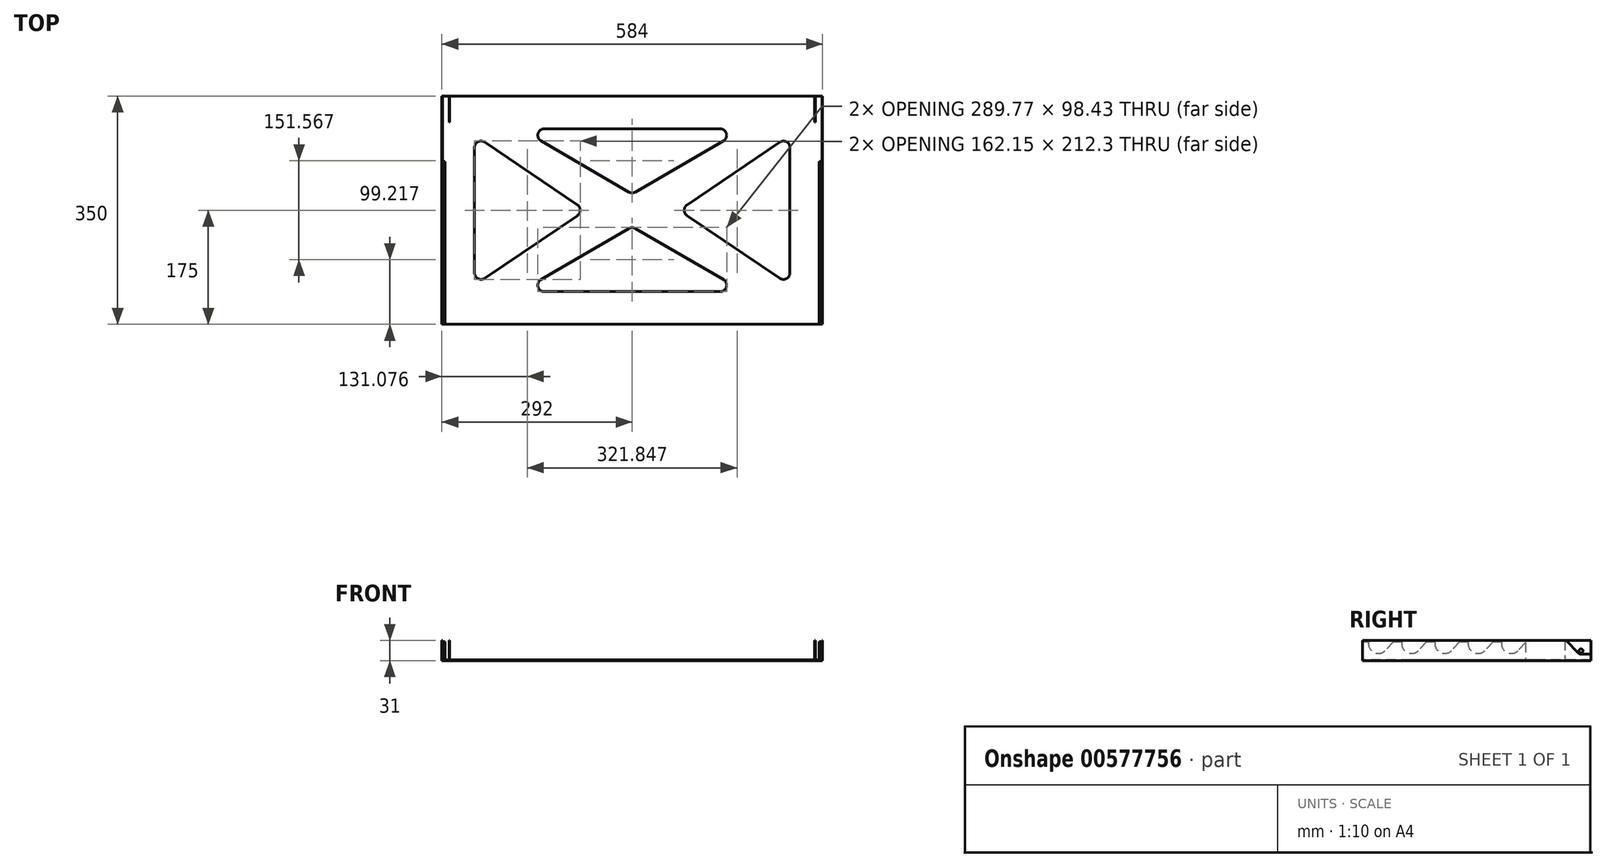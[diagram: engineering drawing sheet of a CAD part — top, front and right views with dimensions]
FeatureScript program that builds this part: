
annotation { "Feature Type Name" : "Feature", "Feature Type Description" : "" }
export const myFeature = defineFeature(function(context is Context, id is Id, definition is map)
    precondition{}
    {
        {
            var Q0;
            Q0=qCreatedBy(makeId("Top.planeOp"),FACE);
            var sketch = newSketch(context, id + "F0", { "sketchPlane" : qUnion([Q0])});
            skLineSegment(sketch, "E0.bottom", {"start": v(-292, 151.73) * mm, "end": v(292, 151.73) * mm});
            skLineSegment(sketch, "E0.top", {"start": v(-292, -198.27) * mm, "end": v(292, -198.27) * mm});
            skLineSegment(sketch, "E0.left", {"start": v(-292, 151.73) * mm, "end": v(-292, -198.27) * mm});
            skLineSegment(sketch, "E0.right", {"start": v(292, 151.73) * mm, "end": v(292, -198.27) * mm});
            skSolve(sketch);
        }
        {
            var Q0;
            Q0 = qSketchRegion(id + "F0", true);
            extrude(context, id + "F1", {"entities" : qUnion([Q0]), "depth" : 1 * mm, "offsetDistance" : 25 * mm});
        }
        {
            var Q0;
            Q0=makeQuery(id+"F1.opExtrude","CAP_FACE",FACE,{"disambiguationData":[OSD([sQuery(id+"F0.wireOp",EDGE,"E0.bottom"),sQuery(id+"F0.wireOp",EDGE,"E0.top"),sQuery(id+"F0.wireOp",EDGE,"E0.left"),sQuery(id+"F0.wireOp",EDGE,"E0.right")])],"isStart":false});
            var sketch = newSketch(context, id + "F2", { "sketchPlane" : qUnion([Q0])});
            skLineSegment(sketch, "E1.bottom", {"start": v(-292, 151.73) * mm, "end": v(-291, 151.73) * mm});
            skLineSegment(sketch, "E1.top", {"start": v(-292, -198.27) * mm, "end": v(-291, -198.27) * mm});
            skLineSegment(sketch, "E1.left", {"start": v(-292, 151.73) * mm, "end": v(-292, -198.27) * mm});
            skLineSegment(sketch, "E1.right", {"start": v(-291, 151.73) * mm, "end": v(-291, -198.27) * mm});
            skLineSegment(sketch, "E2.bottom", {"start": v(292, 151.73) * mm, "end": v(291, 151.73) * mm});
            skLineSegment(sketch, "E2.top", {"start": v(292, -198.27) * mm, "end": v(291, -198.27) * mm});
            skLineSegment(sketch, "E2.left", {"start": v(292, 151.73) * mm, "end": v(292, -198.27) * mm});
            skLineSegment(sketch, "E2.right", {"start": v(291, 151.73) * mm, "end": v(291, -198.27) * mm});
            skSolve(sketch);
        }
        {
            var Q0;
            Q0 = qSketchRegion(id + "F2", true);
            extrude(context, id + "F3", {"entities" : qUnion([Q0]), "operationType" : NewBodyOperationType.ADD, "depth" : 30 * mm, "offsetDistance" : 25 * mm});
        }
        {
            var Q0;
            Q0=makeQuery(id+"F3.boolean.opBoolean","MERGE",FACE,{"derivedFrom":[makeQuery(id+"F1.opExtrude","SWEPT_FACE",FACE,{"disambiguationData":[OSD([sQuery(id+"F0.wireOp",EDGE,"E0.left")])]}),makeQuery(id+"F3.opExtrude","SWEPT_FACE",FACE,{"disambiguationData":[OSD([sQuery(id+"F2.wireOp",EDGE,"E1.left")])]})]});
            var sketch = newSketch(context, id + "F4", { "sketchPlane" : qUnion([Q0])});
            skCircle(sketch, "E3", {"center": v(-136.73, 15) * mm, "radius": 5 * mm});
            skLineSegment(sketch, "E4", {"start": v(-136.73, 15) * mm, "end": v(-136.73, 10) * mm});
            skLineSegment(sketch, "E5", {"start": v(-136.73, 10) * mm, "end": v(-151.73, 10) * mm});
            skLineSegment(sketch, "E6", {"start": v(-151.73, 10) * mm, "end": v(-151.73, 31) * mm});
            skLineSegment(sketch, "E7", {"start": v(-136.73, 15) * mm, "end": v(-120.73, 31) * mm});
            skLineSegment(sketch, "E8", {"start": v(-120.73, 31) * mm, "end": v(-151.73, 31) * mm});
            skLineSegment(sketch, "E9", {"start": v(-133.04, 11.62) * mm, "end": v(-113.67, 31) * mm});
            skSolve(sketch);
        }
        {
            var Q0;
            Q0 = qSketchRegion(id + "F4", true);
            var Q1;
            {var subQ0=sQuery(id+"F4.wireOp",EDGE,"E9");Q1=makeQuery(id+"F4.imprint","IMPRINT",FACE,{"disambiguationData":[TD([[makeQuery(id+"F4.imprint","IMPRINT",EDGE,{"derivedFrom":subQ0}),1.0]])]});}
            extrude(context, id + "F5", {"entities" : qUnion([Q0, Q1]), "operationType" : NewBodyOperationType.REMOVE, "oppositeDirection" : true, "depth" : 645 * mm, "offsetDistance" : 25 * mm});
        }
        {
            var Q0;
            Q0=makeQuery(id+"F1.opExtrude","CAP_FACE",FACE,{"disambiguationData":[OSD([sQuery(id+"F0.wireOp",EDGE,"E0.bottom"),sQuery(id+"F0.wireOp",EDGE,"E0.top"),sQuery(id+"F0.wireOp",EDGE,"E0.left"),sQuery(id+"F0.wireOp",EDGE,"E0.right")])],"isStart":false});
            var sketch = newSketch(context, id + "F6", { "sketchPlane" : qUnion([Q0])});
            skLineSegment(sketch, "E10.bottom", {"start": v(-281, 151.73) * mm, "end": v(-280, 151.73) * mm});
            skLineSegment(sketch, "E10.top", {"start": v(-281, 111.73) * mm, "end": v(-280, 111.73) * mm});
            skLineSegment(sketch, "E10.left", {"start": v(-281, 151.73) * mm, "end": v(-281, 111.73) * mm});
            skLineSegment(sketch, "E10.right", {"start": v(-280, 151.73) * mm, "end": v(-280, 111.73) * mm});
            skLineSegment(sketch, "E11.bottom", {"start": v(281, 151.73) * mm, "end": v(280, 151.73) * mm});
            skLineSegment(sketch, "E11.top", {"start": v(281, 111.73) * mm, "end": v(280, 111.73) * mm});
            skLineSegment(sketch, "E11.left", {"start": v(281, 151.73) * mm, "end": v(281, 111.73) * mm});
            skLineSegment(sketch, "E11.right", {"start": v(280, 151.73) * mm, "end": v(280, 111.73) * mm});
            skSolve(sketch);
        }
        {
            var Q0;
            Q0 = qSketchRegion(id + "F6", true);
            extrude(context, id + "F7", {"entities" : qUnion([Q0]), "operationType" : NewBodyOperationType.ADD, "depth" : 30 * mm, "offsetDistance" : 25 * mm});
        }
        {
            var Q0;
            Q0=makeQuery(id+"F7.opExtrude","SWEPT_FACE",FACE,{"disambiguationData":[OSD([sQuery(id+"F6.wireOp",EDGE,"E10.left")])]});
            var sketch = newSketch(context, id + "F8", { "sketchPlane" : qUnion([Q0])});
            skCircle(sketch, "E12", {"center": v(-136.73, 15) * mm, "radius": 3 * mm});
            skSolve(sketch);
        }
        {
            var Q0;
            Q0 = qSketchRegion(id + "F8", true);
            extrude(context, id + "F9", {"entities" : qUnion([Q0]), "operationType" : NewBodyOperationType.REMOVE, "oppositeDirection" : true, "depth" : 565 * mm, "offsetDistance" : 25 * mm});
        }
        {
            var Q0;
            Q0=makeQuery(id+"F1.opExtrude","CAP_FACE",FACE,{"disambiguationData":[OSD([sQuery(id+"F0.wireOp",EDGE,"E0.bottom"),sQuery(id+"F0.wireOp",EDGE,"E0.top"),sQuery(id+"F0.wireOp",EDGE,"E0.left"),sQuery(id+"F0.wireOp",EDGE,"E0.right")])],"isStart":false});
            var sketch = newSketch(context, id + "F10", { "sketchPlane" : qUnion([Q0])});
            skLineSegment(sketch, "E13.bottom", {"start": v(-290, -198.27) * mm, "end": v(-287, -198.27) * mm});
            skLineSegment(sketch, "E13.top", {"start": v(-290, 51.73) * mm, "end": v(-287, 51.73) * mm});
            skLineSegment(sketch, "E13.left", {"start": v(-290, -198.27) * mm, "end": v(-290, 51.73) * mm});
            skLineSegment(sketch, "E13.right", {"start": v(-287, -198.27) * mm, "end": v(-287, 51.73) * mm});
            skLineSegment(sketch, "E14.bottom", {"start": v(290, -198.27) * mm, "end": v(287, -198.27) * mm});
            skLineSegment(sketch, "E14.top", {"start": v(290, 51.73) * mm, "end": v(287, 51.73) * mm});
            skLineSegment(sketch, "E14.left", {"start": v(290, -198.27) * mm, "end": v(290, 51.73) * mm});
            skLineSegment(sketch, "E14.right", {"start": v(287, -198.27) * mm, "end": v(287, 51.73) * mm});
            skSolve(sketch);
        }
        {
            var Q0;
            Q0 = qSketchRegion(id + "F10", true);
            extrude(context, id + "F11", {"entities" : qUnion([Q0]), "operationType" : NewBodyOperationType.ADD, "depth" : 28 * mm, "offsetDistance" : 25 * mm});
        }
        {
            var Q0;
            Q0=qCreatedBy(makeId("Right.planeOp"),FACE);
            var sketch = newSketch(context, id + "F12", { "sketchPlane" : qUnion([Q0])});
            skCircle(sketch, "E15", {"center": v(-174.38, 26) * mm, "radius": 15 * mm});
            skLineSegment(sketch, "E16", {"start": v(-163.45, 15.73) * mm, "end": v(-125.93, 55.64) * mm});
            skLineSegment(sketch, "E17", {"start": v(-125.93, 55.64) * mm, "end": v(-178.3, 40.48) * mm});
            skCircle(sketch, "E18.1.0.0", {"center": v(-123.38, 26) * mm, "radius": 15 * mm});
            skLineSegment(sketch, "E18.1.0.1", {"start": v(-112.45, 15.73) * mm, "end": v(-74.93, 55.64) * mm});
            skLineSegment(sketch, "E18.1.0.2", {"start": v(-74.93, 55.64) * mm, "end": v(-127.3, 40.48) * mm});
            skCircle(sketch, "E18.2.0.0", {"center": v(-72.38, 26) * mm, "radius": 15 * mm});
            skLineSegment(sketch, "E18.2.0.1", {"start": v(-61.45, 15.73) * mm, "end": v(-23.93, 55.64) * mm});
            skLineSegment(sketch, "E18.2.0.2", {"start": v(-23.93, 55.64) * mm, "end": v(-76.3, 40.48) * mm});
            skCircle(sketch, "E18.3.0.0", {"center": v(-21.38, 26) * mm, "radius": 15 * mm});
            skLineSegment(sketch, "E18.3.0.1", {"start": v(-10.45, 15.73) * mm, "end": v(27.07, 55.64) * mm});
            skLineSegment(sketch, "E18.3.0.2", {"start": v(27.07, 55.64) * mm, "end": v(-25.3, 40.48) * mm});
            skCircle(sketch, "E18.4.0.0", {"center": v(29.62, 26) * mm, "radius": 15 * mm});
            skLineSegment(sketch, "E18.4.0.1", {"start": v(40.55, 15.73) * mm, "end": v(78.07, 55.64) * mm});
            skLineSegment(sketch, "E18.4.0.2", {"start": v(78.07, 55.64) * mm, "end": v(25.7, 40.48) * mm});
            skLineSegment(sketch, "E18.direction1", {"start": v(-174.38, 26) * mm, "end": v(-123.38, 26) * mm, "construction": true});
            skSolve(sketch);
        }
        {
            var Q0;
            Q0 = qSketchRegion(id + "F12", true);
            extrude(context, id + "F13", {"entities" : qUnion([Q0]), "operationType" : NewBodyOperationType.REMOVE, "endBound" : BoundingType.SYMMETRIC, "oppositeDirection" : true, "depth" : 582 * mm, "offsetDistance" : 25 * mm});
        }
        {
            var Q0;
            Q0=makeQuery(id+"F1.opExtrude","CAP_FACE",FACE,{"disambiguationData":[OSD([sQuery(id+"F0.wireOp",EDGE,"E0.bottom"),sQuery(id+"F0.wireOp",EDGE,"E0.top"),sQuery(id+"F0.wireOp",EDGE,"E0.left"),sQuery(id+"F0.wireOp",EDGE,"E0.right")])],"isStart":false});
            var sketch = newSketch(context, id + "F14", { "sketchPlane" : qUnion([Q0])});
            skLineSegment(sketch, "E19", {"start": v(-139.93, 83.09) * mm, "end": v(-5.03, 4.65) * mm});
            skLineSegment(sketch, "E20", {"start": v(5.03, 4.65) * mm, "end": v(139.93, 83.09) * mm});
            skLineSegment(sketch, "E21", {"start": v(134.9, 101.73) * mm, "end": v(-134.9, 101.73) * mm});
            skLineSegment(sketch, "E22", {"start": v(-139.93, -129.62) * mm, "end": v(-5.03, -51.2) * mm});
            skLineSegment(sketch, "E23", {"start": v(5.03, -51.2) * mm, "end": v(139.93, -129.62) * mm});
            skLineSegment(sketch, "E24", {"start": v(134.9, -148.27) * mm, "end": v(-134.9, -148.27) * mm});
            skLineSegment(sketch, "E25", {"start": v(-226.4, 81.18) * mm, "end": v(-84.24, -14.99) * mm});
            skLineSegment(sketch, "E26", {"start": v(-84.24, -31.55) * mm, "end": v(-226.4, -127.71) * mm});
            skLineSegment(sketch, "E27", {"start": v(-242, -119.43) * mm, "end": v(-242, 72.9) * mm});
            skLineSegment(sketch, "E28", {"start": v(84.24, -14.99) * mm, "end": v(226.4, 81.18) * mm});
            skLineSegment(sketch, "E29", {"start": v(242, 72.9) * mm, "end": v(242, -119.43) * mm});
            skLineSegment(sketch, "E30", {"start": v(226.4, -127.71) * mm, "end": v(84.24, -31.55) * mm});
            skPoint(sketch, "E31.visualSharp", {"position": v(-172, 101.73) * mm});
            skArc(sketch, "E31.filletArc", {"start": v(-134.9, 101.73) * mm, "mid": v(-144.56, 94.33) * mm, "end": v(-139.93, 83.09) * mm});
            skPoint(sketch, "E32.visualSharp", {"position": v(172, 101.73) * mm});
            skArc(sketch, "E32.filletArc", {"start": v(139.93, 83.09) * mm, "mid": v(144.56, 94.33) * mm, "end": v(134.9, 101.73) * mm});
            skPoint(sketch, "E33.visualSharp", {"position": v(0, 1.73) * mm});
            skArc(sketch, "E33.filletArc", {"start": v(-5.03, 4.65) * mm, "mid": v(0, 3.3) * mm, "end": v(5.03, 4.65) * mm});
            skPoint(sketch, "E34.visualSharp", {"position": v(242, 91.73) * mm});
            skArc(sketch, "E34.filletArc", {"start": v(242, 72.9) * mm, "mid": v(236.69, 81.73) * mm, "end": v(226.4, 81.18) * mm});
            skPoint(sketch, "E35.visualSharp", {"position": v(72, -23.27) * mm});
            skArc(sketch, "E35.filletArc", {"start": v(84.24, -14.99) * mm, "mid": v(79.85, -23.27) * mm, "end": v(84.24, -31.55) * mm});
            skPoint(sketch, "E36.visualSharp", {"position": v(242, -138.27) * mm});
            skArc(sketch, "E36.filletArc", {"start": v(226.4, -127.71) * mm, "mid": v(236.69, -128.26) * mm, "end": v(242, -119.43) * mm});
            skPoint(sketch, "E37.visualSharp", {"position": v(172, -148.27) * mm});
            skArc(sketch, "E37.filletArc", {"start": v(134.9, -148.27) * mm, "mid": v(144.56, -140.87) * mm, "end": v(139.93, -129.62) * mm});
            skPoint(sketch, "E38.visualSharp", {"position": v(0, -48.27) * mm});
            skArc(sketch, "E38.filletArc", {"start": v(5.03, -51.2) * mm, "mid": v(0, -49.84) * mm, "end": v(-5.03, -51.2) * mm});
            skPoint(sketch, "E39.visualSharp", {"position": v(-172, -148.27) * mm});
            skArc(sketch, "E39.filletArc", {"start": v(-139.93, -129.62) * mm, "mid": v(-144.56, -140.87) * mm, "end": v(-134.9, -148.27) * mm});
            skPoint(sketch, "E40.visualSharp", {"position": v(-72, -23.27) * mm});
            skArc(sketch, "E40.filletArc", {"start": v(-84.24, -31.55) * mm, "mid": v(-79.85, -23.27) * mm, "end": v(-84.24, -14.99) * mm});
            skPoint(sketch, "E41.visualSharp", {"position": v(-242, -138.27) * mm});
            skArc(sketch, "E41.filletArc", {"start": v(-242, -119.43) * mm, "mid": v(-236.69, -128.26) * mm, "end": v(-226.4, -127.71) * mm});
            skPoint(sketch, "E42.visualSharp", {"position": v(-242, 91.73) * mm});
            skArc(sketch, "E42.filletArc", {"start": v(-226.4, 81.18) * mm, "mid": v(-236.69, 81.73) * mm, "end": v(-242, 72.9) * mm});
            skSolve(sketch);
        }
        {
            var Q0;
            Q0 = qSketchRegion(id + "F14", true);
            extrude(context, id + "F15", {"entities" : qUnion([Q0]), "operationType" : NewBodyOperationType.REMOVE, "oppositeDirection" : true, "depth" : 25 * mm, "offsetDistance" : 25 * mm});
        }
    });
